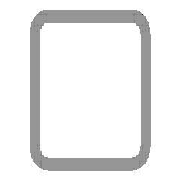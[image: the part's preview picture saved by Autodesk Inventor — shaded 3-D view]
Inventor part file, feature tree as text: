
AUTODESK INVENTOR PART (.ipt)
format: ipt  version: 2025.1 (Build 291241020, 241B)  size: 134,144 bytes
history: native  units: mm (DEFAULTED — no unit token found)
features: other x4, sketch x1, plane x1
ambient origin geometry x8: Origin, YZ Plane, XZ Plane, XY Plane, X Axis, Y Axis, Z Axis, Center Point
bodies: Solid1 (feature_tree), Body (feature_tree)
feature tree (6):
  parser-record x1  (decoder bookkeeping rows leaked as tree rows — omitted from the tree; the rows remain in map.json)
  other  "Driven Length"
  other  "Start Plane"
  other  "End Plane"
  sketch  "Sketch3"  dims[d3=1150.0mm d4=0.0mm d7=8.0mm d9=100.0mm d11=100.0mm d12=4.0mm d13=50.0mm d14=1200.0mm d15=50.0mm d16=50.0mm d17=90.0deg d18=1150.0mm]
  plane  "Work Plane3"
